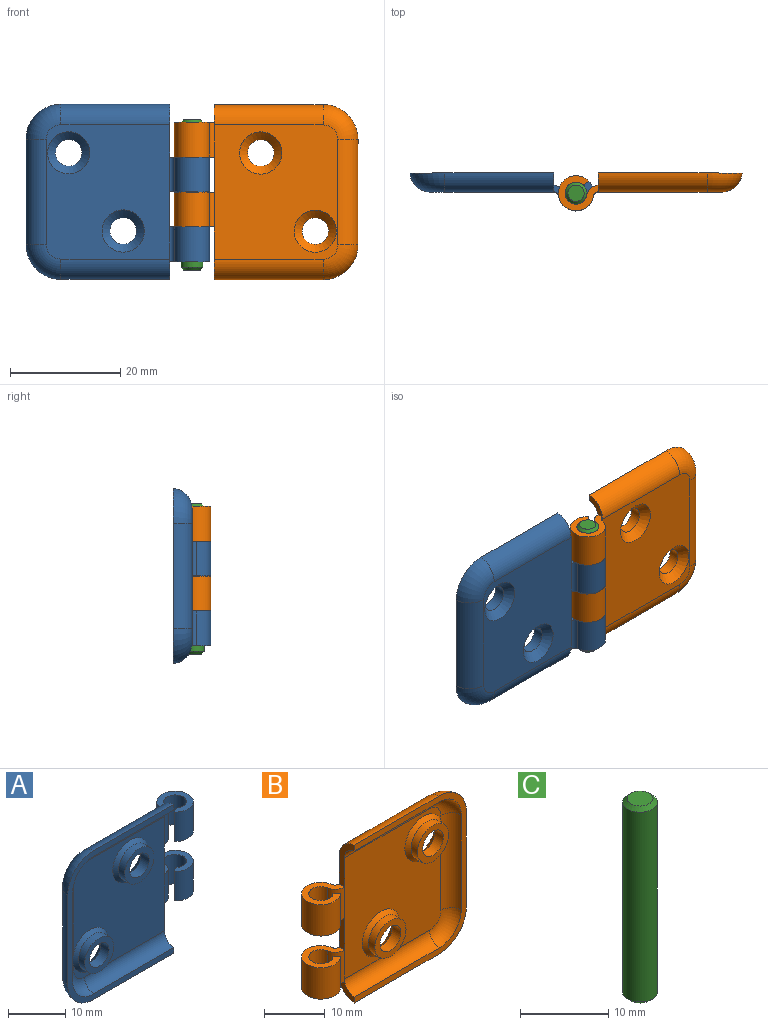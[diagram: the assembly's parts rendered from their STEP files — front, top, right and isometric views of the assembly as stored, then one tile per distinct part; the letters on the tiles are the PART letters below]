
ASSEMBLY  parts=3 mates=2
PART A: 41 faces, bbox 33.3x7.1x31.8 mm
  f0: cylinder r=1.98mm len=6.3mm, axis (0,0,1), area 66.5mm2, adj f36,f37,f39,f40
  f1: cylinder r=3.18mm len=6.37mm, axis (0,0,1), area 107.4mm2, adj f35,f36,f39,f40
  f2: cylinder r=1.98mm len=6.3mm, axis (0,0,1), area 66.5mm2, adj f31,f32,f33,f34
  f3: cylinder r=3.18mm len=6.37mm, axis (0,0,1), area 107.4mm2, adj f30,f31,f33,f34
  f4: cone r=4.68mm half-angle=45deg, axis (0,1,0), area 25.3mm2, adj f5,f24,f27
  f5: cylinder r=3.61mm len=7.23mm, axis (0,1,0), area 34.3mm2, adj f4,f14
  f6: cone r=4.68mm half-angle=45deg, axis (0,1,0), area 25.3mm2, adj f7,f24
  f7: cylinder r=3.61mm len=7.23mm, axis (0,1,0), area 34.3mm2, adj f6,f17
  f8: cone r=3.83mm half-angle=45deg, axis (0,1,0), area 39.4mm2, adj f9,f18
  f9: cylinder r=2.41mm len=4.83mm, axis (0,1,0), area 30.5mm2, adj f8,f14
  f10: cone r=3.83mm half-angle=45deg, axis (0,1,0), area 39.4mm2, adj f11,f18
  f11: cylinder r=2.41mm len=4.83mm, axis (0,1,0), area 30.5mm2, adj f10,f17
  f12: plane 6.4x1.2mm, normal (1,0,0), area 7.7mm2, adj f18,f24,f34,f39
  f13: plane 9.58x3.43mm, normal (1,0,0), area 12.6mm2, adj f15,f18,f19,f24,f25,f33
  f14: plane 7.23x7.23mm, normal (0,-1,0), area 22.7mm2, adj f5,f9
  f15: plane 31.8x26.1mm, normal (0,-1,0), area 92.4mm2, adj f13,f16,f19,f20,f21,f22,f23,f25
  f16: plane 3.69x3.4mm, normal (1,0,0), area 5mm2, adj f15,f23,f29,f37,f40
  f17: plane 7.23x7.23mm, normal (0,-1,0), area 22.7mm2, adj f7,f11
  f18: plane 24.42x22.41mm, normal (0,1,0), area 451.8mm2, adj f8,f10,f12,f13,f19,f20,f21,f22
  f19: cylinder r=3.7mm len=19.75mm, axis (-1,0,0), area 109.4mm2, adj f13,f15,f18,f20
  f20: torus R=2.66mm, axis (0,1,0), area 43.1mm2, adj f15,f18,f19,f21
  f21: cylinder r=3.7mm len=19.1mm, axis (0,0,1), area 105.8mm2, adj f15,f18,f20,f22
  f22: torus R=2.66mm, axis (0,1,0), area 43.1mm2, adj f15,f18,f21,f23
  f23: cylinder r=3.7mm len=19.75mm, axis (1,0,0), area 109.4mm2, adj f15,f16,f18,f22,f38
  f24: plane 24.42x22.41mm, normal (0,-1,0), area 426.9mm2, adj f4,f6,f12,f13,f25,f26,f27,f28
  f25: cylinder r=2.5mm len=19.75mm, axis (-1,0,0), area 72.2mm2, adj f13,f15,f24,f26
  f26: torus R=2.66mm, axis (0,1,0), area 24mm2, adj f15,f24,f25,f27
  f27: cylinder r=2.5mm len=19.1mm, axis (0,0,1), area 69.3mm2, adj f4,f15,f24,f26,f28
  f28: torus R=2.66mm, axis (0,1,0), area 24mm2, adj f15,f24,f27,f29
  f29: cylinder r=2.5mm len=19.75mm, axis (1,0,0), area 72.2mm2, adj f15,f16,f24,f28
  f30: cylinder r=0.94mm len=6.3mm, axis (0,0,1), area 8.3mm2, adj f3,f18,f33,f34
  f31: plane 6.3x0.92mm, normal (-0.64,0.76,0), area 7.6mm2, adj f2,f3,f33,f34
  f32: cylinder r=2.14mm len=6.3mm, axis (0,0,1), area 18.9mm2, adj f2,f24,f33,f34
  f33: plane 7.25x6.37mm, normal (0,0,-1), area 19.2mm2, adj f2,f3,f13,f30,f31,f32
  f34: plane 7.25x6.37mm, normal (0,0,1), area 19.2mm2, adj f2,f3,f12,f30,f31,f32
  f35: cylinder r=0.94mm len=6.3mm, axis (0,0,1), area 8.3mm2, adj f1,f18,f38,f39,f40
  f36: plane 6.3x0.92mm, normal (-0.64,0.76,0), area 7.6mm2, adj f0,f1,f39,f40
  f37: cylinder r=2.14mm len=6.3mm, axis (0,0,1), area 18.9mm2, adj f0,f16,f24,f39,f40
  f38: plane 0.46x0.03mm, normal (-1,0,0), area 0mm2, adj f23,f35,f40
  f39: plane 7.25x6.37mm, normal (0,0,-1), area 19.2mm2, adj f0,f1,f12,f35,f36,f37
  f40: plane 7.25x6.37mm, normal (0,0,1), area 19.2mm2, adj f0,f1,f16,f35,f36,f37,f38
PART B: 41 faces, bbox 33.3x7.1x31.8 mm
  f0: cylinder r=1.98mm len=6.3mm, axis (0,0,-1), area 66.5mm2, adj f36,f37,f39,f40
  f1: cylinder r=3.18mm len=6.37mm, axis (0,0,-1), area 107.4mm2, adj f35,f36,f39,f40
  f2: cylinder r=1.98mm len=6.3mm, axis (0,0,-1), area 66.5mm2, adj f31,f32,f33,f34
  f3: cylinder r=3.18mm len=6.37mm, axis (0,0,-1), area 107.4mm2, adj f30,f31,f33,f34
  f4: cone r=4.68mm half-angle=45deg, axis (0,1,0), area 25.3mm2, adj f5,f24,f27
  f5: cylinder r=3.61mm len=7.23mm, axis (0,1,0), area 34.3mm2, adj f4,f14
  f6: cone r=4.68mm half-angle=45deg, axis (0,1,0), area 25.3mm2, adj f7,f24
  f7: cylinder r=3.61mm len=7.23mm, axis (0,1,0), area 34.3mm2, adj f6,f17
  f8: cone r=3.83mm half-angle=45deg, axis (0,1,0), area 39.4mm2, adj f9,f18
  f9: cylinder r=2.41mm len=4.83mm, axis (0,1,0), area 30.5mm2, adj f8,f14
  f10: cone r=3.83mm half-angle=45deg, axis (0,1,0), area 39.4mm2, adj f11,f18
  f11: cylinder r=2.41mm len=4.83mm, axis (0,1,0), area 30.5mm2, adj f10,f17
  f12: plane 6.4x1.2mm, normal (-1,0,0), area 7.7mm2, adj f18,f24,f34,f39
  f13: plane 9.58x3.43mm, normal (-1,0,0), area 12.6mm2, adj f15,f18,f19,f24,f25,f33
  f14: plane 7.23x7.23mm, normal (0,-1,0), area 22.7mm2, adj f5,f9
  f15: plane 31.8x26.1mm, normal (0,-1,0), area 92.4mm2, adj f13,f16,f19,f20,f21,f22,f23,f25
  f16: plane 3.69x3.4mm, normal (-1,0,0), area 5mm2, adj f15,f23,f29,f37,f40
  f17: plane 7.23x7.23mm, normal (0,-1,0), area 22.7mm2, adj f7,f11
  f18: plane 24.42x22.41mm, normal (0,1,0), area 451.8mm2, adj f8,f10,f12,f13,f19,f20,f21,f22
  f19: cylinder r=3.7mm len=19.75mm, axis (1,0,0), area 109.4mm2, adj f13,f15,f18,f20
  f20: torus R=2.66mm, axis (0,1,0), area 43.1mm2, adj f15,f18,f19,f21
  f21: cylinder r=3.7mm len=19.1mm, axis (0,0,-1), area 105.8mm2, adj f15,f18,f20,f22
  f22: torus R=2.66mm, axis (0,1,0), area 43.1mm2, adj f15,f18,f21,f23
  f23: cylinder r=3.7mm len=19.75mm, axis (-1,0,0), area 109.4mm2, adj f15,f16,f18,f22,f38
  f24: plane 24.42x22.41mm, normal (0,-1,0), area 426.9mm2, adj f4,f6,f12,f13,f25,f26,f27,f28
  f25: cylinder r=2.5mm len=19.75mm, axis (1,0,0), area 72.2mm2, adj f13,f15,f24,f26
  f26: torus R=2.66mm, axis (0,1,0), area 24mm2, adj f15,f24,f25,f27
  f27: cylinder r=2.5mm len=19.1mm, axis (0,0,-1), area 69.3mm2, adj f4,f15,f24,f26,f28
  f28: torus R=2.66mm, axis (0,1,0), area 24mm2, adj f15,f24,f27,f29
  f29: cylinder r=2.5mm len=19.75mm, axis (-1,0,0), area 72.2mm2, adj f15,f16,f24,f28
  f30: cylinder r=0.94mm len=6.3mm, axis (0,0,-1), area 8.3mm2, adj f3,f18,f33,f34
  f31: plane 6.3x0.92mm, normal (0.64,0.76,0), area 7.6mm2, adj f2,f3,f33,f34
  f32: cylinder r=2.14mm len=6.3mm, axis (0,0,-1), area 18.9mm2, adj f2,f24,f33,f34
  f33: plane 7.25x6.37mm, normal (0,0,1), area 19.2mm2, adj f2,f3,f13,f30,f31,f32
  f34: plane 7.25x6.37mm, normal (0,0,-1), area 19.2mm2, adj f2,f3,f12,f30,f31,f32
  f35: cylinder r=0.94mm len=6.3mm, axis (0,0,-1), area 8.3mm2, adj f1,f18,f38,f39,f40
  f36: plane 6.3x0.92mm, normal (0.64,0.76,0), area 7.6mm2, adj f0,f1,f39,f40
  f37: cylinder r=2.14mm len=6.3mm, axis (0,0,-1), area 18.9mm2, adj f0,f16,f24,f39,f40
  f38: plane 0.46x0.03mm, normal (1,0,0), area 0mm2, adj f23,f35,f40
  f39: plane 7.25x6.37mm, normal (0,0,1), area 19.2mm2, adj f0,f1,f12,f35,f36,f37
  f40: plane 7.25x6.37mm, normal (0,0,-1), area 19.2mm2, adj f0,f1,f16,f35,f36,f37,f38
PART C: 5 faces, bbox 4x4x27.4 mm
  f0: cone r=1.48mm half-angle=45deg, axis (0,0,-1), area 7.8mm2, adj f2,f3
  f1: cone r=1.98mm half-angle=45deg, axis (0,0,1), area 7.8mm2, adj f2,f4
  f2: cylinder r=1.98mm len=26.37mm, axis (0,0,-1), area 328.7mm2, adj f0,f1
  f3: plane 2.95x2.95mm, normal (0,0,1), area 6.8mm2, adj f0
  f4: plane 2.95x2.95mm, normal (0,0,-1), area 6.8mm2, adj f1
PLACE A rot(axis=(1,0,0),180deg) t=(-8.37,0.03,7.12)mm
PLACE B rot(axis=(1,0,0),180deg) t=(-8.37,0.03,7.07)mm
PLACE C rot(axis=(1,0,0),180deg) t=(-8.37,0.03,6.56)mm
MATE revolute B.f3 <-> C.f0  axis (0,0,1) through (-8.37,-0.22,19.74)mm
MATE revolute A.f0 <-> B.f3  axis (0,0,1) through (-8.37,-0.22,13.44)mm
